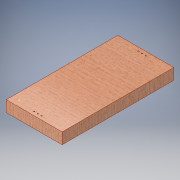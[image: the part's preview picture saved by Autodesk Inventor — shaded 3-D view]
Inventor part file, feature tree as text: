
AUTODESK INVENTOR PART (.ipt)
format: ipt  version: 2019 (Build 230136000, 136)  size: 143,872 bytes
history: native  units: mm
features: sketch x4, hole x2, other x1, extrude x1
ambient origin geometry x8: Origin, YZ Plane, XZ Plane, XY Plane, X Axis, Y Axis, Z Axis, Center Point
bodies: Body1 (feature_tree)
feature tree (8):
  other  "ソリッド1"
  extrude  "押し出し1"  Depth=150.0mm
  sketch  "スケッチ2"
  sketch  "スケッチ3"
  sketch  "スケッチ4"
  hole  "穴1"  [1 undecoded]
  hole  "穴2"  [1 undecoded]
  sketch  "スケッチ1"
note: 2 required parameter values undecoded (feature->parameter linkage not recoverable at this tier; creation-order binding heuristic only, values carry confidence <= 0.55)
